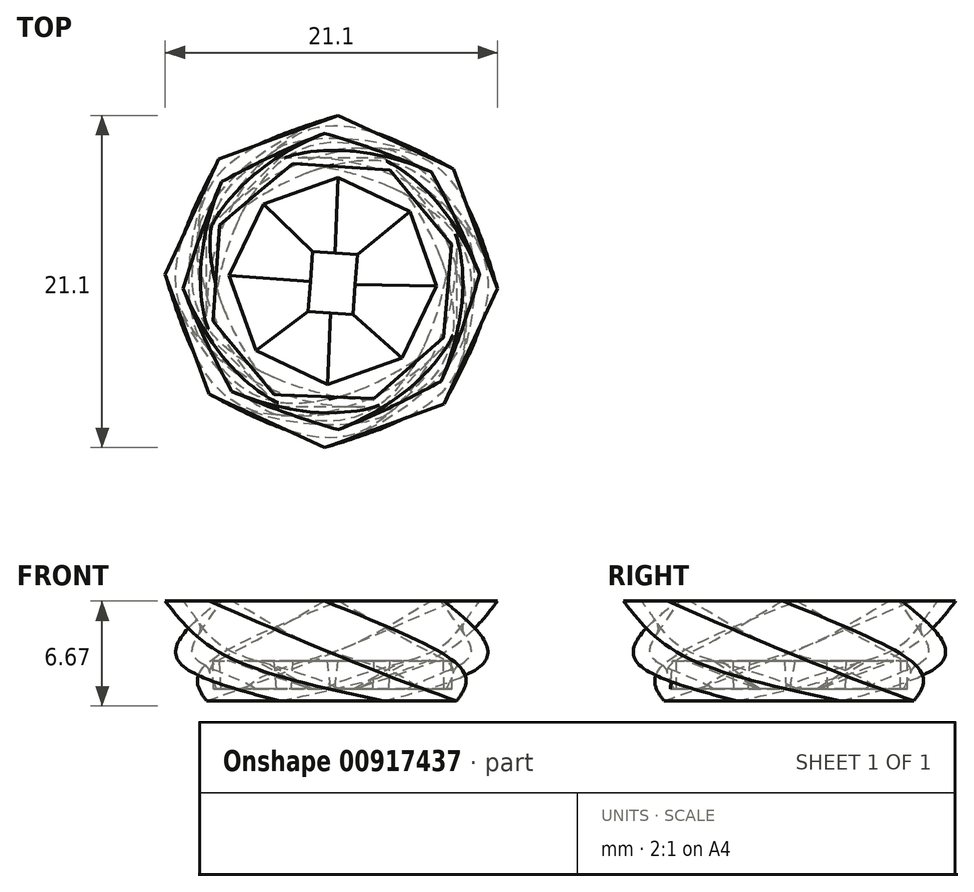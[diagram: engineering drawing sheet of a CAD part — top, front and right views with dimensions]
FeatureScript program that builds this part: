
annotation { "Feature Type Name" : "Feature", "Feature Type Description" : "" }
export const myFeature = defineFeature(function(context is Context, id is Id, definition is map)
    precondition{}
    {
        {
            var Q0;
            Q0=qCreatedBy(makeId("Top.planeOp"),FACE);
            var sketch = newSketch(context, id + "F0", { "sketchPlane" : qUnion([Q0])});
            skLineSegment(sketch, "E0", {"start": v(0, 0) * mm, "end": v(-12.7, 0) * mm, "construction": true});
            skLineSegment(sketch, "E1", {"start": v(0, 0) * mm, "end": v(0, -12.7) * mm, "construction": true});
            skLineSegment(sketch, "E2", {"start": v(0, -25.4) * mm, "end": v(-12.7, -25.4) * mm, "construction": true});
            skLineSegment(sketch, "E3", {"start": v(-25.35, 0) * mm, "end": v(-25.35, -12.7) * mm, "construction": true});
            skLineSegment(sketch, "E4", {"start": v(0, 0) * mm, "end": v(-25.23, -25.31) * mm, "construction": true});
            skLineSegment(sketch, "E5", {"start": v(0, -25.4) * mm, "end": v(-25.35, 0) * mm, "construction": true});
            skCircle(sketch, "E6.cCircle", {"center": v(-12.67, -12.7) * mm, "radius": 7.93 * mm, "construction": true});
            skLineSegment(sketch, "E6.0", {"start": v(-15.95, -4.78) * mm, "end": v(-9.38, -4.78) * mm});
            skLineSegment(sketch, "E6.1", {"start": v(-9.38, -4.78) * mm, "end": v(-4.73, -9.42) * mm});
            skLineSegment(sketch, "E6.2", {"start": v(-4.73, -9.42) * mm, "end": v(-4.73, -16) * mm});
            skLineSegment(sketch, "E6.3", {"start": v(-4.73, -16) * mm, "end": v(-9.38, -20.64) * mm});
            skLineSegment(sketch, "E6.4", {"start": v(-9.38, -20.64) * mm, "end": v(-15.95, -20.64) * mm});
            skLineSegment(sketch, "E6.5", {"start": v(-15.95, -20.64) * mm, "end": v(-20.6, -16) * mm});
            skLineSegment(sketch, "E6.6", {"start": v(-20.6, -16) * mm, "end": v(-20.6, -9.42) * mm});
            skLineSegment(sketch, "E6.7", {"start": v(-20.6, -9.42) * mm, "end": v(-15.95, -4.78) * mm});
            skPoint(sketch, "E6.0.midPoint", {"position": v(-12.67, -4.78) * mm});
            skSolve(sketch);
        }
        {
            var Q0;
            Q0=qCreatedBy(makeId("Top.planeOp"),FACE);
            cPlane(context, id + "F1", {"entities" : qUnion([Q0]), "cplaneType" : CPlaneType.OFFSET, "offset" : 2.54 * mm, "width" : 152.4 * mm, "height" : 152.4 * mm});
        }
        {
            var Q0;
            Q0=qCreatedBy(id+"F1.planeOp",FACE);
            var sketch = newSketch(context, id + "F2", { "sketchPlane" : qUnion([Q0])});
            skCircle(sketch, "E7.cCircle", {"center": v(-12.65, -12.67) * mm, "radius": 9.07 * mm, "construction": true});
            skLineSegment(sketch, "E7.0", {"start": v(-18.69, -20.42) * mm, "end": v(-22.4, -13.88) * mm});
            skLineSegment(sketch, "E7.1", {"start": v(-22.4, -13.88) * mm, "end": v(-20.4, -6.64) * mm});
            skLineSegment(sketch, "E7.2", {"start": v(-20.4, -6.64) * mm, "end": v(-13.87, -2.93) * mm});
            skLineSegment(sketch, "E7.3", {"start": v(-13.87, -2.93) * mm, "end": v(-6.62, -4.93) * mm});
            skLineSegment(sketch, "E7.4", {"start": v(-6.62, -4.93) * mm, "end": v(-2.91, -11.46) * mm});
            skLineSegment(sketch, "E7.5", {"start": v(-2.91, -11.46) * mm, "end": v(-4.91, -18.7) * mm});
            skLineSegment(sketch, "E7.6", {"start": v(-4.91, -18.7) * mm, "end": v(-11.44, -22.41) * mm});
            skLineSegment(sketch, "E7.7", {"start": v(-11.44, -22.41) * mm, "end": v(-18.69, -20.42) * mm});
            skPoint(sketch, "E7.0.midPoint", {"position": v(-20.54, -17.15) * mm});
            skSolve(sketch);
        }
        {
            var Q0;
            Q0=qCreatedBy(id+"F1.planeOp",FACE);
            cPlane(context, id + "F3", {"entities" : qUnion([Q0]), "cplaneType" : CPlaneType.OFFSET, "offset" : 3.8 * mm, "width" : 152.4 * mm, "height" : 152.4 * mm});
        }
        {
            var Q0;
            Q0=qCreatedBy(id+"F3.planeOp",FACE);
            var sketch = newSketch(context, id + "F4", { "sketchPlane" : qUnion([Q0])});
            skCircle(sketch, "E8.cCircle", {"center": v(-12.68, -12.66) * mm, "radius": 9.75 * mm, "construction": true});
            skLineSegment(sketch, "E8.0", {"start": v(-13.12, -23.2) * mm, "end": v(-20.45, -19.81) * mm});
            skLineSegment(sketch, "E8.1", {"start": v(-20.45, -19.81) * mm, "end": v(-23.23, -12.23) * mm});
            skLineSegment(sketch, "E8.2", {"start": v(-23.23, -12.23) * mm, "end": v(-19.83, -4.9) * mm});
            skLineSegment(sketch, "E8.3", {"start": v(-19.83, -4.9) * mm, "end": v(-12.25, -2.11) * mm});
            skLineSegment(sketch, "E8.4", {"start": v(-12.25, -2.11) * mm, "end": v(-4.91, -5.5) * mm});
            skLineSegment(sketch, "E8.5", {"start": v(-4.91, -5.5) * mm, "end": v(-2.13, -13.1) * mm});
            skLineSegment(sketch, "E8.6", {"start": v(-2.13, -13.1) * mm, "end": v(-5.53, -20.43) * mm});
            skLineSegment(sketch, "E8.7", {"start": v(-5.53, -20.43) * mm, "end": v(-13.12, -23.2) * mm});
            skPoint(sketch, "E8.0.midPoint", {"position": v(-16.78, -21.51) * mm});
            skSolve(sketch);
        }
        {
            var Q0;
            Q0=makeQuery(id+"F0.imprint","IMPRINT",FACE,{"disambiguationData":[TD([[makeQuery(id+"F0.imprint","IMPRINT",EDGE,{"derivedFrom":sQuery(id+"F0.wireOp",EDGE,"E6.0")}),-1.0]])]});
            var Q1;
            Q1=makeQuery(id+"F2.imprint","IMPRINT",FACE,{"disambiguationData":[TD([[makeQuery(id+"F2.imprint","IMPRINT",EDGE,{"derivedFrom":sQuery(id+"F2.wireOp",EDGE,"E7.0")}),-1.0]])]});
            var Q2;
            Q2=makeQuery(id+"F4.imprint","IMPRINT",FACE,{"disambiguationData":[TD([[makeQuery(id+"F4.imprint","IMPRINT",EDGE,{"derivedFrom":sQuery(id+"F4.wireOp",EDGE,"E8.0")}),-1.0]])]});
            var Q3;
            Q3=sQuery(id+"F0.wireOp",VERTEX,"E6.4.end");
            var Q4;
            Q4=sQuery(id+"F2.wireOp",VERTEX,"E7.0.end");
            var Q5;
            Q5=sQuery(id+"F4.wireOp",VERTEX,"E8.2.end");
            loft(context, id + "F5", {"sheetProfilesArray" : [{ "sheetProfileEntities" : qUnion([Q0]) }, { "sheetProfileEntities" : qUnion([Q1]) }, { "sheetProfileEntities" : qUnion([Q2]) }], "trimGuidesByProfiles" : true, "matchConnections" : true, "connections" : [{ "connectionEntities" : qUnion([Q3, Q4, Q5]), "connectionEdgeQueries" : qUnion([]), "connectionEdgeParameters" : [] }]});
        }
        {
            var Q0;
            Q0=makeQuery(id+"F5.opLoft","CAP_FACE",FACE,{"disambiguationData":[OSD([makeQuery(id+"F4.imprint","IMPRINT",FACE,{"disambiguationData":[TD([[makeQuery(id+"F4.imprint","IMPRINT",EDGE,{"derivedFrom":sQuery(id+"F4.wireOp",EDGE,"E8.0")}),-1.0]])]})])],"isStart":true});
            shell(context, id + "F6", {"entities" : qUnion([Q0]), "thickness" : 0.76 * mm});
        }
        {
            var Q0;
            Q0=qCreatedBy(id+"F1.planeOp",FACE);
            var sketch = newSketch(context, id + "F7", { "sketchPlane" : qUnion([Q0])});
            skLineSegment(sketch, "E9", {"start": v(-19.78, -9.06) * mm, "end": v(-5.06, -10.3) * mm, "construction": true});
            skLineSegment(sketch, "E10", {"start": v(-5.06, -10.3) * mm, "end": v(-20.2, -15.18) * mm, "construction": true});
            skLineSegment(sketch, "E11", {"start": v(-20.2, -15.18) * mm, "end": v(-5.23, -16.25) * mm, "construction": true});
            skLineSegment(sketch, "E12", {"start": v(-5.23, -16.25) * mm, "end": v(-15.11, -5.17) * mm, "construction": true});
            skLineSegment(sketch, "E13", {"start": v(-15.11, -5.17) * mm, "end": v(-8.95, -5.6) * mm, "construction": true});
            skLineSegment(sketch, "E14", {"start": v(-8.95, -5.6) * mm, "end": v(-9.96, -20.1) * mm, "construction": true});
            skLineSegment(sketch, "E15", {"start": v(-9.96, -20.1) * mm, "end": v(-15.11, -5.17) * mm, "construction": true});
            skLineSegment(sketch, "E16", {"start": v(-16.31, -19.84) * mm, "end": v(-15.11, -5.17) * mm, "construction": true});
            skLineSegment(sketch, "E17", {"start": v(-8.95, -5.6) * mm, "end": v(-5.06, -10.3) * mm, "construction": true});
            skLineSegment(sketch, "E18", {"start": v(-15.11, -5.17) * mm, "end": v(-19.78, -9.06) * mm, "construction": true});
            skLineSegment(sketch, "E19", {"start": v(-19.78, -9.06) * mm, "end": v(-20.2, -15.18) * mm, "construction": true});
            skLineSegment(sketch, "E20", {"start": v(-20.2, -15.18) * mm, "end": v(-16.31, -19.84) * mm, "construction": true});
            skLineSegment(sketch, "E21", {"start": v(-16.31, -19.84) * mm, "end": v(-9.96, -20.1) * mm, "construction": true});
            skLineSegment(sketch, "E22", {"start": v(-5.06, -10.3) * mm, "end": v(-5.56, -16.22) * mm, "construction": true});
            skLineSegment(sketch, "E23", {"start": v(-13.14, -19.97) * mm, "end": v(-12.03, -5.38) * mm, "construction": true});
            skLineSegment(sketch, "E24", {"start": v(-20, -12.12) * mm, "end": v(-5.3, -13.15) * mm, "construction": true});
            skLineSegment(sketch, "E25", {"start": v(-20.2, -15.18) * mm, "end": v(-16.31, -19.84) * mm});
            skLineSegment(sketch, "E26", {"start": v(-16.31, -19.84) * mm, "end": v(-9.96, -20.1) * mm});
            skLineSegment(sketch, "E27", {"start": v(-5.56, -16.22) * mm, "end": v(-5.06, -10.3) * mm});
            skLineSegment(sketch, "E28", {"start": v(-5.06, -10.3) * mm, "end": v(-8.95, -5.6) * mm});
            skLineSegment(sketch, "E29", {"start": v(-8.95, -5.6) * mm, "end": v(-15.11, -5.17) * mm});
            skLineSegment(sketch, "E30", {"start": v(-15.11, -5.17) * mm, "end": v(-19.78, -9.06) * mm});
            skLineSegment(sketch, "E31", {"start": v(-19.78, -9.06) * mm, "end": v(-20.2, -15.18) * mm});
            skPoint(sketch, "E32.0.midPoint", {"position": v(-12.15, -6.9) * mm});
            skLineSegment(sketch, "E33", {"start": v(-9.96, -20.1) * mm, "end": v(-5.56, -16.22) * mm});
            skSolve(sketch);
        }
        {
            var Q0;
            Q0=qCreatedBy(makeId("Top.planeOp"),FACE);
            cPlane(context, id + "F8", {"entities" : qUnion([Q0]), "cplaneType" : CPlaneType.OFFSET, "offset" : 0.76 * mm, "width" : 152.4 * mm, "height" : 152.4 * mm});
        }
        {
            var Q0;
            Q0=qCreatedBy(id+"F8.planeOp",FACE);
            var sketch = newSketch(context, id + "F9", { "sketchPlane" : qUnion([Q0])});
            skLineSegment(sketch, "E34", {"start": v(-12.6, -12.75) * mm, "end": v(-12.06, -5.15) * mm, "construction": true});
            skLineSegment(sketch, "E35", {"start": v(-12.6, -12.75) * mm, "end": v(-12.46, -10.85) * mm, "construction": true});
            skLineSegment(sketch, "E36", {"start": v(-11.17, -12.85) * mm, "end": v(-11.03, -10.95) * mm});
            skLineSegment(sketch, "E37", {"start": v(-12.46, -10.85) * mm, "end": v(-11.03, -10.95) * mm});
            skLineSegment(sketch, "E38", {"start": v(-12.46, -10.85) * mm, "end": v(-13.88, -10.75) * mm});
            skLineSegment(sketch, "E39", {"start": v(-12.6, -12.75) * mm, "end": v(-14.02, -12.65) * mm, "construction": true});
            skLineSegment(sketch, "E40", {"start": v(-13.88, -10.75) * mm, "end": v(-14.02, -12.65) * mm});
            skLineSegment(sketch, "E41", {"start": v(-12.6, -12.75) * mm, "end": v(-11.17, -12.85) * mm, "construction": true});
            skLineSegment(sketch, "E42", {"start": v(-12.6, -12.75) * mm, "end": v(-12.73, -14.65) * mm, "construction": true});
            skLineSegment(sketch, "E43", {"start": v(-11.17, -12.85) * mm, "end": v(-11.3, -14.75) * mm});
            skLineSegment(sketch, "E44", {"start": v(-14.02, -12.65) * mm, "end": v(-14.15, -14.55) * mm});
            skLineSegment(sketch, "E45", {"start": v(-14.15, -14.55) * mm, "end": v(-11.3, -14.75) * mm});
            skLineSegment(sketch, "E46", {"start": v(-19.8, -9.17) * mm, "end": v(-15.11, -5.08) * mm, "construction": true});
            skLineSegment(sketch, "E47", {"start": v(-15.11, -5.08) * mm, "end": v(-9.13, -5.5) * mm, "construction": true});
            skLineSegment(sketch, "E48", {"start": v(-9.13, -5.5) * mm, "end": v(-5.16, -10.14) * mm, "construction": true});
            skLineSegment(sketch, "E49", {"start": v(-5.16, -10.14) * mm, "end": v(-5.59, -16.17) * mm, "construction": true});
            skLineSegment(sketch, "E50", {"start": v(-10.06, -20.18) * mm, "end": v(-16.22, -19.9) * mm, "construction": true});
            skLineSegment(sketch, "E51", {"start": v(-16.22, -19.9) * mm, "end": v(-20.22, -15.3) * mm, "construction": true});
            skLineSegment(sketch, "E52", {"start": v(-20.22, -15.3) * mm, "end": v(-19.8, -9.17) * mm, "construction": true});
            skSolve(sketch);
        }
        {
            var Q0;
            Q0=qCreatedBy(id+"F8.planeOp",FACE);
            var sketch = newSketch(context, id + "F10", { "sketchPlane" : qUnion([Q0])});
            skLineSegment(sketch, "E53", {"start": v(-19.69, -9.1) * mm, "end": v(-15.21, -5.16) * mm});
            skLineSegment(sketch, "E54", {"start": v(-15.21, -5.16) * mm, "end": v(-9, -5.62) * mm});
            skLineSegment(sketch, "E55", {"start": v(-9, -5.62) * mm, "end": v(-5.02, -10.22) * mm});
            skLineSegment(sketch, "E56", {"start": v(-5.02, -10.22) * mm, "end": v(-5.53, -16.2) * mm});
            skLineSegment(sketch, "E57", {"start": v(-5.53, -16.2) * mm, "end": v(-10.02, -20.22) * mm});
            skLineSegment(sketch, "E58", {"start": v(-10.02, -20.22) * mm, "end": v(-16.18, -19.84) * mm});
            skLineSegment(sketch, "E59", {"start": v(-16.18, -19.84) * mm, "end": v(-20.17, -15.26) * mm});
            skLineSegment(sketch, "E60", {"start": v(-20.17, -15.26) * mm, "end": v(-19.69, -9.1) * mm});
            skSolve(sketch);
        }
        {
            var Q0;
            Q0 = qSketchRegion(id + "F10", true);
            var Q1;
            Q1 = qSketchRegion(id + "F7", true);
            loft(context, id + "F11", {"sheetProfilesArray" : [{ "sheetProfileEntities" : qUnion([Q0]) }, { "sheetProfileEntities" : qUnion([Q1]) }]});
        }
        {
            var Q0;
            Q0=qCreatedBy(id+"F1.planeOp",FACE);
            var sketch = newSketch(context, id + "F12", { "sketchPlane" : qUnion([Q0])});
            skCircle(sketch, "E61.cCircle", {"center": v(-12.6, -12.62) * mm, "radius": 6.58 * mm, "construction": true});
            skLineSegment(sketch, "E61.0", {"start": v(-12.25, -6.04) * mm, "end": v(-7.7, -8.2) * mm});
            skLineSegment(sketch, "E61.1", {"start": v(-7.7, -8.2) * mm, "end": v(-6.02, -12.96) * mm});
            skLineSegment(sketch, "E61.2", {"start": v(-6.02, -12.96) * mm, "end": v(-8.18, -17.5) * mm});
            skLineSegment(sketch, "E61.3", {"start": v(-8.18, -17.5) * mm, "end": v(-12.93, -19.2) * mm});
            skLineSegment(sketch, "E61.4", {"start": v(-12.93, -19.2) * mm, "end": v(-17.48, -17.03) * mm});
            skLineSegment(sketch, "E61.5", {"start": v(-17.48, -17.03) * mm, "end": v(-19.17, -12.28) * mm});
            skLineSegment(sketch, "E61.6", {"start": v(-19.17, -12.28) * mm, "end": v(-17, -7.73) * mm});
            skLineSegment(sketch, "E61.7", {"start": v(-17, -7.73) * mm, "end": v(-12.25, -6.04) * mm});
            skSolve(sketch);
        }
        {
            var Q1;
            Q1 = qSketchRegion(id + "F9", true);
            var Q2;
            Q2 = qSketchRegion(id + "F12", true);
            loft(context, id + "F13", {"operationType" : NewBodyOperationType.REMOVE, "sheetProfilesArray" : [{ "sheetProfileEntities" : qUnion([Q1]) }, { "sheetProfileEntities" : qUnion([Q2]) }]});
        }
    });
